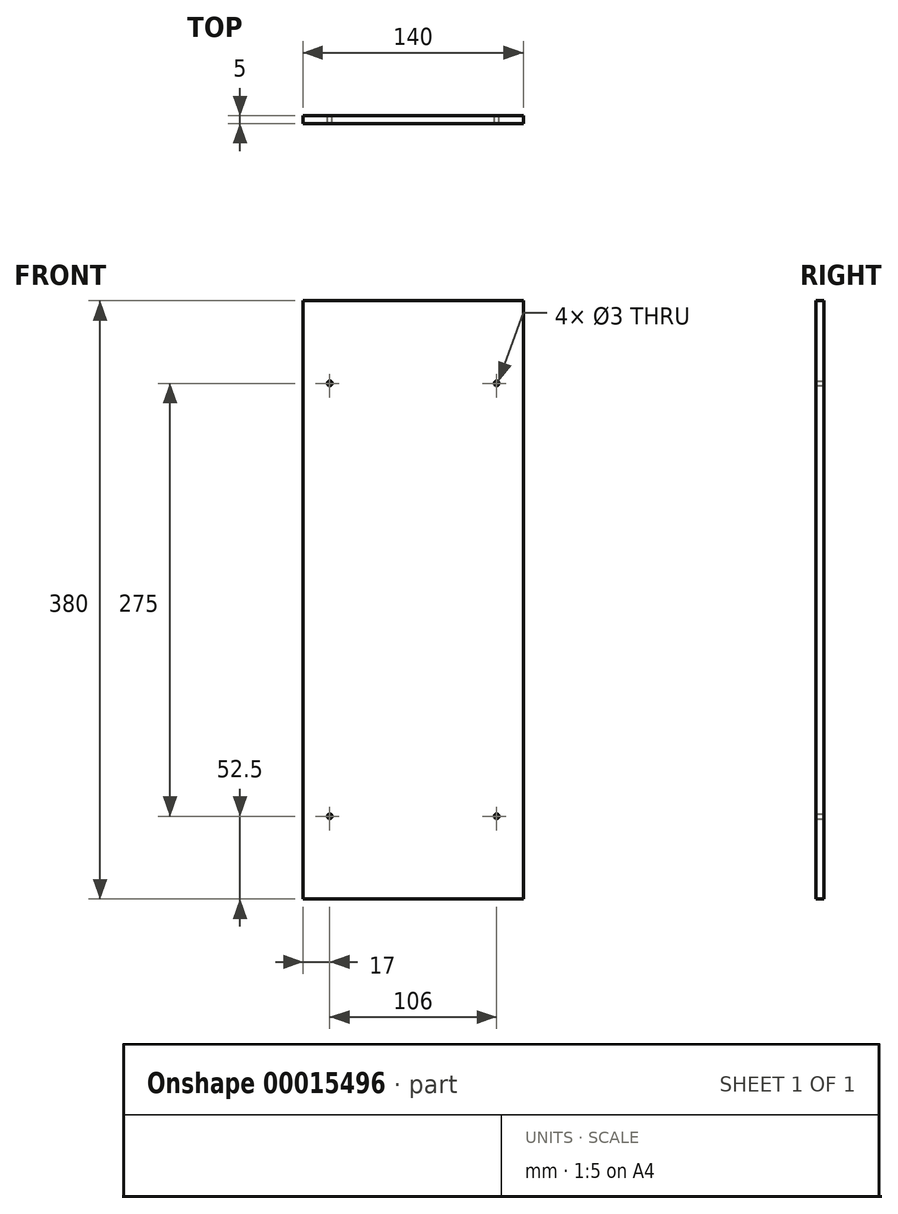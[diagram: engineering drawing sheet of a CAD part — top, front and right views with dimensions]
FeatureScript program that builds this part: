
annotation { "Feature Type Name" : "Feature", "Feature Type Description" : "" }
export const myFeature = defineFeature(function(context is Context, id is Id, definition is map)
    precondition{}
    {
        {
            var Q0;
            Q0=qCreatedBy(makeId("Front.planeOp"),FACE);
            var sketch = newSketch(context, id + "F0", { "sketchPlane" : qUnion([Q0])});
            skLineSegment(sketch, "E0.rect.bottom", {"start": v(70, 190) * mm, "end": v(-70, 190) * mm});
            skLineSegment(sketch, "E0.rect.top", {"start": v(70, -190) * mm, "end": v(-70, -190) * mm});
            skLineSegment(sketch, "E0.rect.left", {"start": v(70, 190) * mm, "end": v(70, -190) * mm});
            skLineSegment(sketch, "E0.rect.right", {"start": v(-70, 190) * mm, "end": v(-70, -190) * mm});
            skPoint(sketch, "E0.rect.middle", {"position": v(0, 0) * mm});
            skSolve(sketch);
        }
        {
            var Q0;
            Q0=qSketchRegion(id+"F0",true);
            extrude(context, id + "F1", {"entities" : qUnion([Q0]), "depth" : 5 * mm});
        }
        {
            var Q0;
            Q0=qCreatedBy(makeId("Front.planeOp"),FACE);
            var sketch = newSketch(context, id + "F2", { "sketchPlane" : qUnion([Q0])});
            skCircle(sketch, "E1", {"center": v(-53, 137.5) * mm, "radius": 1.5 * mm});
            skLineSegment(sketch, "E2.rect.bottom", {"start": v(-53, 137.5) * mm, "end": v(53, 137.5) * mm, "construction": true});
            skLineSegment(sketch, "E2.rect.top", {"start": v(-53, -137.5) * mm, "end": v(53, -137.5) * mm, "construction": true});
            skLineSegment(sketch, "E2.rect.left", {"start": v(-53, 137.5) * mm, "end": v(-53, -137.5) * mm, "construction": true});
            skLineSegment(sketch, "E2.rect.right", {"start": v(53, 137.5) * mm, "end": v(53, -137.5) * mm, "construction": true});
            skPoint(sketch, "E2.rect.middle", {"position": v(0, 0) * mm});
            skCircle(sketch, "E3", {"center": v(53, 137.5) * mm, "radius": 1.5 * mm});
            skCircle(sketch, "E4", {"center": v(53, -137.5) * mm, "radius": 1.5 * mm});
            skCircle(sketch, "E5", {"center": v(-53, -137.5) * mm, "radius": 1.5 * mm});
            skSolve(sketch);
        }
        {
            var Q0;
            Q0=qSketchRegion(id+"F2",true);
            extrude(context, id + "F3", {"entities" : qUnion([Q0]), "operationType" : NewBodyOperationType.REMOVE, "endBound" : BoundingType.THROUGH_ALL, "depth" : 25 * mm});
        }
    });
